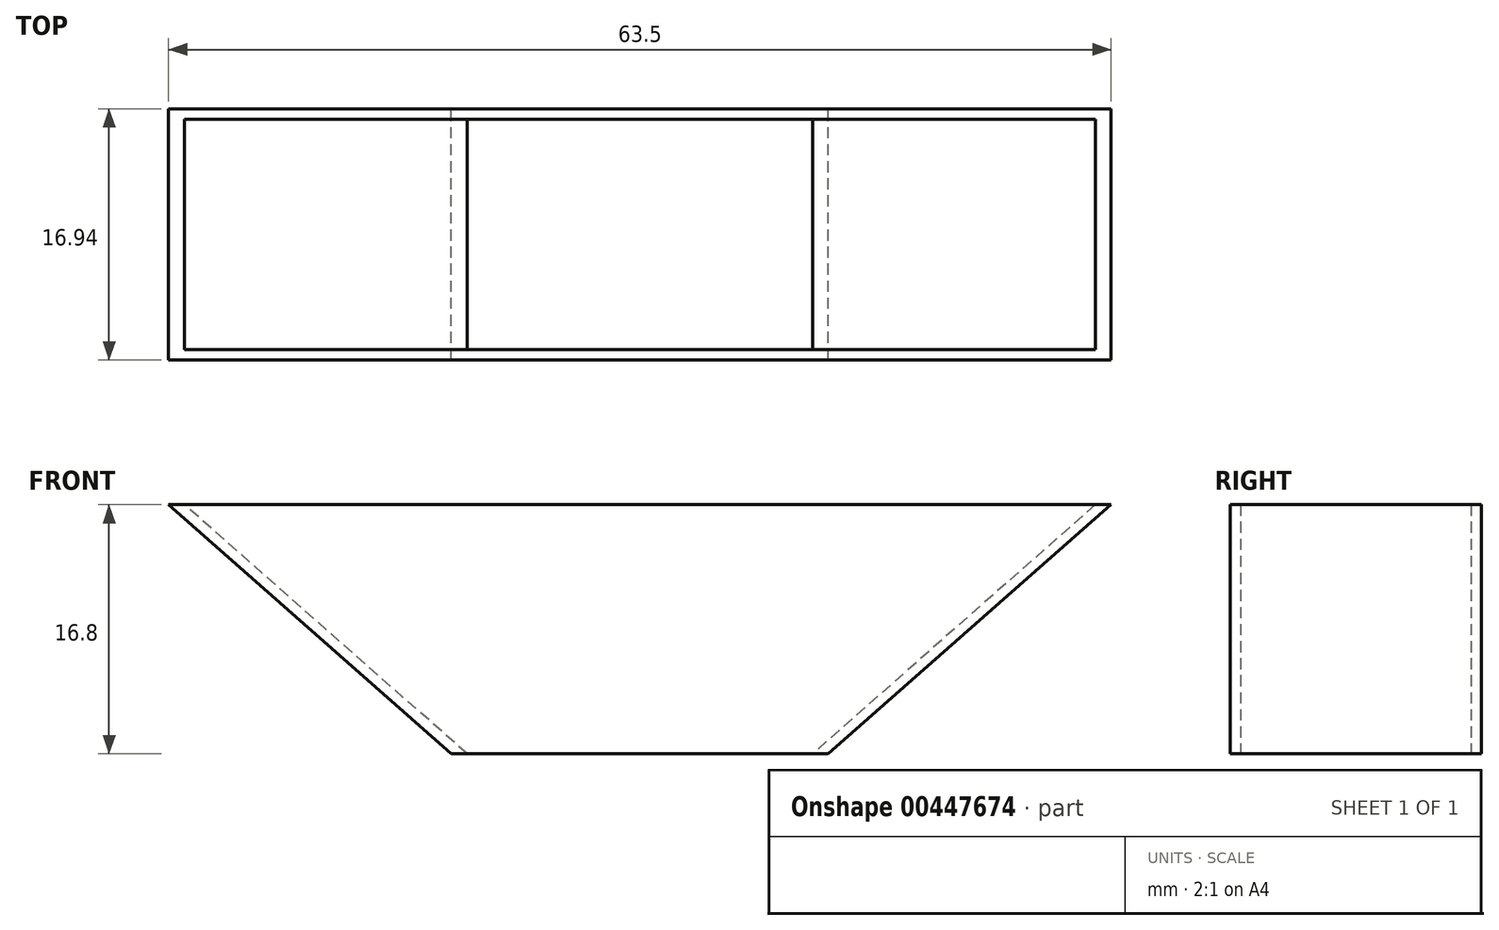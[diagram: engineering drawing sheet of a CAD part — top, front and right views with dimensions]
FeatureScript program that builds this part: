
annotation { "Feature Type Name" : "Feature", "Feature Type Description" : "" }
export const myFeature = defineFeature(function(context is Context, id is Id, definition is map)
    precondition{}
    {
        {
            var Q0;
            Q0=qCreatedBy(makeId("Front.planeOp"),FACE);
            var sketch = newSketch(context, id + "F0", { "sketchPlane" : qUnion([Q0])});
            skLineSegment(sketch, "E0.bottom", {"start": v(25.4, -14.9) * mm, "end": v(0, -14.9) * mm});
            skLineSegment(sketch, "E1", {"start": v(0, -14.9) * mm, "end": v(-19.05, 1.9) * mm});
            skLineSegment(sketch, "E2", {"start": v(-19.05, 1.9) * mm, "end": v(44.45, 1.9) * mm});
            skLineSegment(sketch, "E3", {"start": v(44.45, 1.9) * mm, "end": v(25.4, -14.9) * mm});
            skSolve(sketch);
        }
        {
            var Q0;
            Q0=makeQuery(id+"F0.imprint","IMPRINT",FACE,{"disambiguationData":[TD([[makeQuery(id+"F0.imprint","IMPRINT",EDGE,{"derivedFrom":sQuery(id+"F0.wireOp",EDGE,"E0.bottom")}),-1.0]])]});
            extrude(context, id + "F1", {"entities" : qUnion([Q0]), "endBound" : BoundingType.SYMMETRIC, "depth" : 16.93 * mm});
        }
        {
            var Q0;
            Q0=makeQuery(id+"F1.opExtrude","SWEPT_FACE",FACE,{"disambiguationData":[OSD([sQuery(id+"F0.wireOp",EDGE,"E2")])]});
            var Q1;
            Q1=makeQuery(id+"F1.opExtrude","SWEPT_FACE",FACE,{"disambiguationData":[OSD([sQuery(id+"F0.wireOp",EDGE,"E0.bottom")])]});
            shell(context, id + "F2", {"entities" : qUnion([Q0, Q1]), "thickness" : 0.7 * mm});
        }
    });
